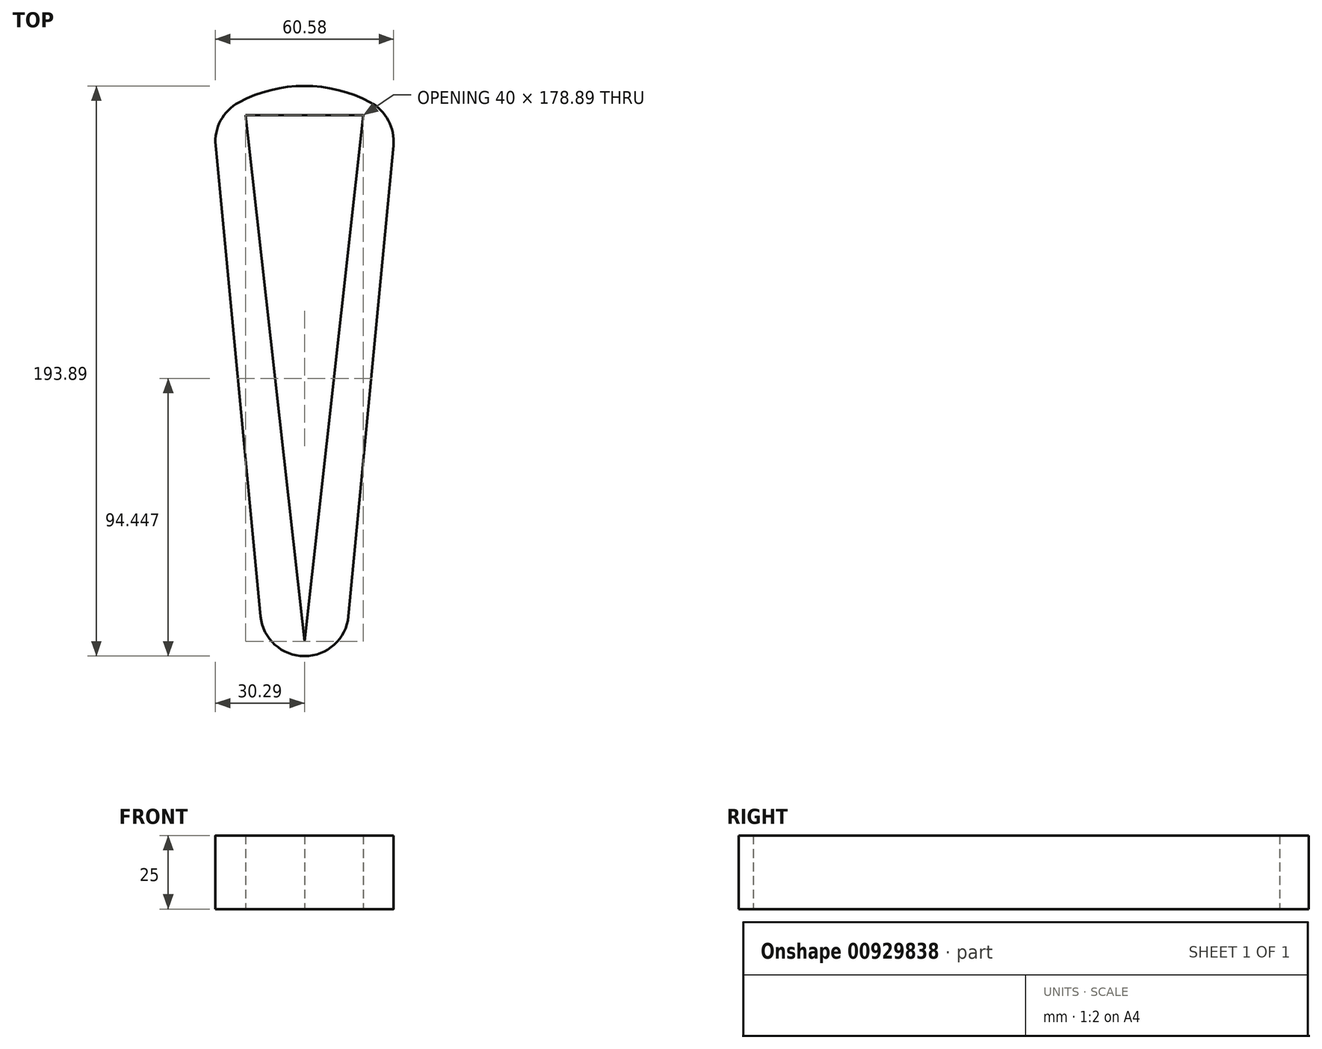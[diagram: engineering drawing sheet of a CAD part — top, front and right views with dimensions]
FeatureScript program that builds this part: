
annotation { "Feature Type Name" : "Feature", "Feature Type Description" : "" }
export const myFeature = defineFeature(function(context is Context, id is Id, definition is map)
    precondition{}
    {
        {
            var Q0;
            Q0=qCreatedBy(makeId("Top.planeOp"),FACE);
            var sketch = newSketch(context, id + "F0", { "sketchPlane" : qUnion([Q0])});
            skCircle(sketch, "E0", {"center": v(-20, 37.5) * mm, "radius": 5 * mm});
            skCircle(sketch, "E1", {"center": v(20, 37.5) * mm, "radius": 5 * mm});
            skCircle(sketch, "E2", {"center": v(0, -141.39) * mm, "radius": 5 * mm});
            skLineSegment(sketch, "E3", {"start": v(-20, 37.5) * mm, "end": v(0, -141.39) * mm});
            skLineSegment(sketch, "E4", {"start": v(20, 37.5) * mm, "end": v(0, -141.39) * mm});
            skLineSegment(sketch, "E5", {"start": v(20, 37.5) * mm, "end": v(-20, 37.5) * mm});
            skLineSegment(sketch, "E6", {"start": v(0, 37.5) * mm, "end": v(0, -141.39) * mm});
            skArc(sketch, "E7", {"start": v(30.23, 27.25) * mm, "mid": v(28.5, 35.77) * mm, "end": v(22.35, 41.91) * mm});
            skArc(sketch, "E8", {"start": v(-22.35, 41.91) * mm, "mid": v(-28.5, 35.77) * mm, "end": v(-30.23, 27.25) * mm});
            skLineSegment(sketch, "E9", {"start": v(-15.3, 28.68) * mm, "end": v(15.3, 28.68) * mm});
            skArc(sketch, "E10", {"start": v(-14.93, -132.81) * mm, "mid": v(0, -146.39) * mm, "end": v(14.93, -132.81) * mm});
            skLineSegment(sketch, "E11", {"start": v(-30.23, 27.25) * mm, "end": v(-14.93, -132.81) * mm});
            skLineSegment(sketch, "E12", {"start": v(30.23, 27.25) * mm, "end": v(14.93, -132.81) * mm});
            skLineSegment(sketch, "E13", {"start": v(0, 47.5) * mm, "end": v(0, 37.5) * mm});
            skArc(sketch, "E14.trimOffspring", {"start": v(22.35, 41.91) * mm, "mid": v(0, 47.5) * mm, "end": v(-22.35, 41.91) * mm});
            skSolve(sketch);
        }
        {
            var Q0;
            {var subQ0=sQuery(id+"F0.wireOp",EDGE,"E8");Q0=makeQuery(id+"F0.imprint","IMPRINT",FACE,{"disambiguationData":[TD([[makeQuery(id+"F0.imprint","IMPRINT",EDGE,{"derivedFrom":subQ0}),1.0]])]});}
            var Q1;
            {var subQ0=sQuery(id+"F0.wireOp",EDGE,"E7");Q1=makeQuery(id+"F0.imprint","IMPRINT",FACE,{"disambiguationData":[TD([[makeQuery(id+"F0.imprint","IMPRINT",EDGE,{"derivedFrom":subQ0}),1.0]])]});}
            var Q2;
            {var subQ0=sQuery(id+"F0.wireOp",EDGE,"E2");var subQ1=makeQuery(id+"F0.imprint","INTERSECT",VERTEX,{"derivedFrom":[subQ0,sQuery(id+"F0.wireOp",EDGE,"E10")]});Q2=makeQuery(id+"F0.imprint","IMPRINT",FACE,{"disambiguationData":[TD([[makeQuery(id+"F0.imprint","IMPRINT",EDGE,{"disambiguationData":[TD([[subQ1,1.0]])],"derivedFrom":subQ0}),1.0]])]});}
            var Q3;
            {var subQ5=sQuery(id+"F0.wireOp",EDGE,"E13");Q3=makeQuery(id+"F0.imprint","IMPRINT",FACE,{"disambiguationData":[TD([[makeQuery(id+"F0.imprint","IMPRINT",EDGE,{"derivedFrom":subQ5}),-1.0]])]});}
            var Q4;
            {var subQ5=sQuery(id+"F0.wireOp",EDGE,"E13");Q4=makeQuery(id+"F0.imprint","IMPRINT",FACE,{"disambiguationData":[TD([[makeQuery(id+"F0.imprint","IMPRINT",EDGE,{"derivedFrom":subQ5}),1.0]])]});}
            var Q5;
            {var subQ2=sQuery(id+"F0.wireOp",EDGE,"E5");var subQ4=sQuery(id+"F0.wireOp",EDGE,"E4");var subQ5=makeQuery(id+"F0.imprint","INTERSECT",VERTEX,{"derivedFrom":[subQ4,subQ2]});Q5=makeQuery(id+"F0.imprint","IMPRINT",FACE,{"disambiguationData":[TD([[makeQuery(id+"F0.imprint","IMPRINT",EDGE,{"disambiguationData":[TD([[subQ5,-1.0]])],"derivedFrom":subQ4}),1.0]])]});}
            var Q6;
            {var subQ2=sQuery(id+"F0.wireOp",EDGE,"E5");var subQ4=sQuery(id+"F0.wireOp",EDGE,"E3");var subQ5=makeQuery(id+"F0.imprint","INTERSECT",VERTEX,{"derivedFrom":[subQ4,subQ2]});Q6=makeQuery(id+"F0.imprint","IMPRINT",FACE,{"disambiguationData":[TD([[makeQuery(id+"F0.imprint","IMPRINT",EDGE,{"disambiguationData":[TD([[subQ5,-1.0]])],"derivedFrom":subQ4}),-1.0]])]});}
            extrude(context, id + "F1", {"entities" : qUnion([Q0, Q1, Q2, Q3, Q4, Q5, Q6]), "depth" : 25 * mm, "offsetDistance" : 25 * mm});
        }
    });
